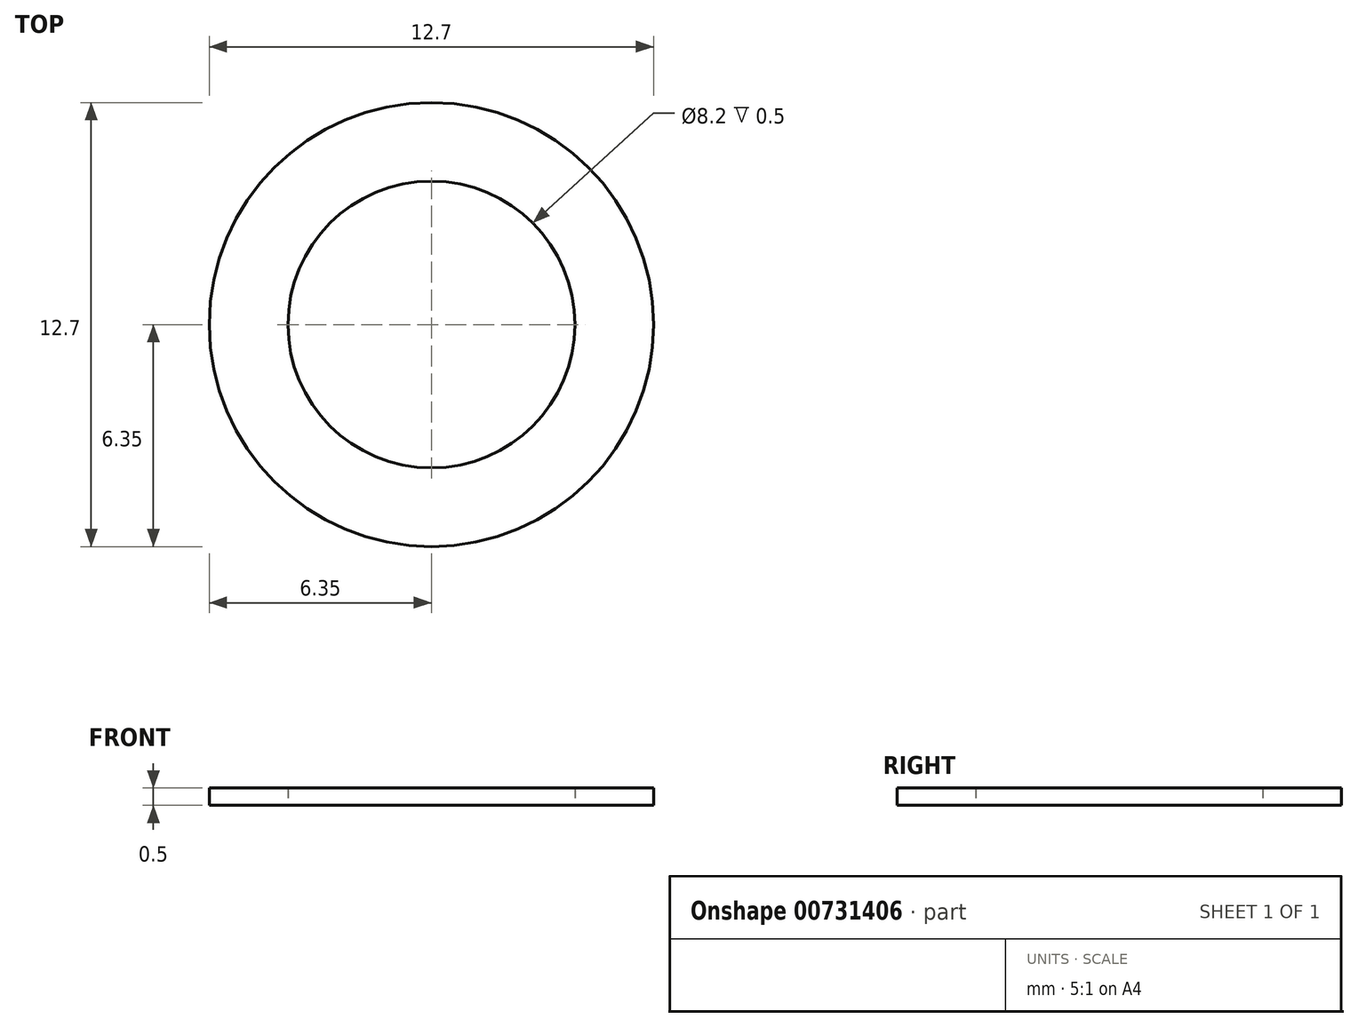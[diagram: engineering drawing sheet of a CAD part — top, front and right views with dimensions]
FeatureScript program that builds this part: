
annotation { "Feature Type Name" : "Feature", "Feature Type Description" : "" }
export const myFeature = defineFeature(function(context is Context, id is Id, definition is map)
    precondition{}
    {
        {
            var Q0;
            Q0=qCreatedBy(makeId("Top.planeOp"),FACE);
            var sketch = newSketch(context, id + "F0", { "sketchPlane" : qUnion([Q0])});
            skCircle(sketch, "E0", {"center": v(0, 0) * mm, "radius": 4.1 * mm});
            skCircle(sketch, "E1", {"center": v(0, 0) * mm, "radius": 6.35 * mm});
            skSolve(sketch);
        }
        {
            var Q0;
            Q0 = qSketchRegion(id + "F0", true);
            extrude(context, id + "F1", {"entities" : qUnion([Q0]), "depth" : .5 * mm, "offsetDistance" : 25 * mm});
        }
    });
